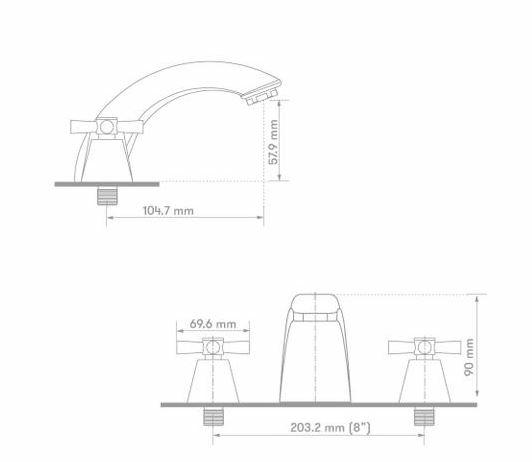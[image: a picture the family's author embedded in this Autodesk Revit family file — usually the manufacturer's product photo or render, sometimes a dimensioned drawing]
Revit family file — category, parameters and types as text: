
# Revit family: 01-3503-11-MEZCLADOR LAVAMANOS 8 FIRENZE CRUZ
name_source: partatom
category: Plumbing Fixtures
revit_build: Autodesk Revit 2018 (Build: 20170223_1515(x64)
units: mm (PartAtom-declared; Revit-internal decimal feet)

## family parameters
Cut with Voids When Loaded = No
Host = Face
OmniClass Number = 23.31.11.00
Part Type = Normal
Room Calculation Point = No
Round Connector Dimension = Use Diameter
Shared = No

## types (1)
- 01-3503-11
    Alto = 113 mm
    Ancho = 274 mm  [stored 0.89895 ft]
    CW Connection = Yes
    Default Elevation = 0 mm  [stored 0 ft]
    Description = MEZCLADOR LAVAMANOS 8 FIRENZE CRUZ
    HW Connection = Yes
    Largo = 127 mm
    Link Ficha Tecnica = http://infotecnica.gricol.com
    Manufacturer = Gricol
    Model = 01-3503-11
    Plastico ABS Cromado = Metal Acero Inoxidable Cromado
    Product Name = MEZCLADOR LAVAMANOS COLECCIÓN PORTOBELLO
    Type Image = GRIFERIA BIMANDO FIRENZE FOTO.jpg
    URL = https://www.gricol.com
    Vent Connection = No
    Waste Connection = No

note: [stored X ft] marks values corroborated as IEEE doubles in the binary element streams (Revit-internal decimal feet)

## geometry (parser evidence)
native form markers: Blend x2, Sweep x8
no freeform markers — native parametric forms only
